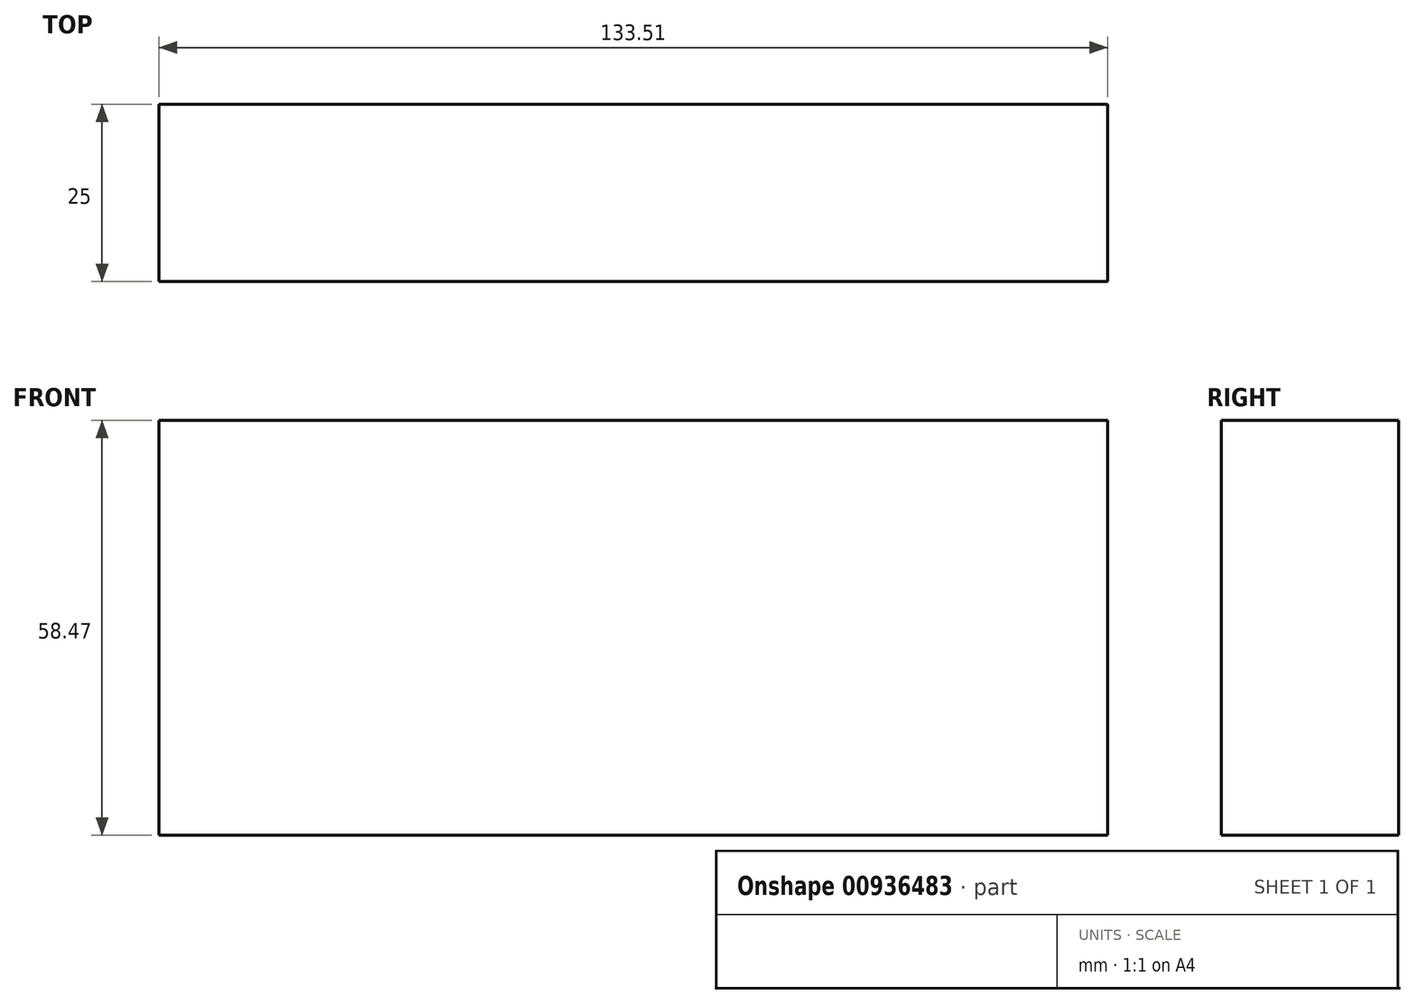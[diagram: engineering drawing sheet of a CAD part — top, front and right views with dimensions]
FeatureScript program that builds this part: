
annotation { "Feature Type Name" : "Feature", "Feature Type Description" : "" }
export const myFeature = defineFeature(function(context is Context, id is Id, definition is map)
    precondition{}
    {
        {
            var Q0;
            Q0=qCreatedBy(makeId("Front.planeOp"),FACE);
            var sketch = newSketch(context, id + "F0", { "sketchPlane" : qUnion([Q0])});
            skLineSegment(sketch, "E0.bottom", {"start": v(-116.79, 40.9) * mm, "end": v(16.72, 40.9) * mm});
            skLineSegment(sketch, "E0.top", {"start": v(-116.79, -17.57) * mm, "end": v(16.72, -17.57) * mm});
            skLineSegment(sketch, "E0.left", {"start": v(-116.79, 40.9) * mm, "end": v(-116.79, -17.57) * mm});
            skLineSegment(sketch, "E0.right", {"start": v(16.72, 40.9) * mm, "end": v(16.72, -17.57) * mm});
            skSolve(sketch);
        }
        {
            var Q0;
            Q0=makeQuery(id+"F0.imprint","IMPRINT",FACE,{"disambiguationData":[TD([[makeQuery(id+"F0.imprint","IMPRINT",EDGE,{"derivedFrom":sQuery(id+"F0.wireOp",EDGE,"E0.bottom")}),-1.0]])]});
            extrude(context, id + "F1", {"entities" : qUnion([Q0]), "depth" : 25 * mm, "offsetDistance" : 25 * mm});
        }
    });
